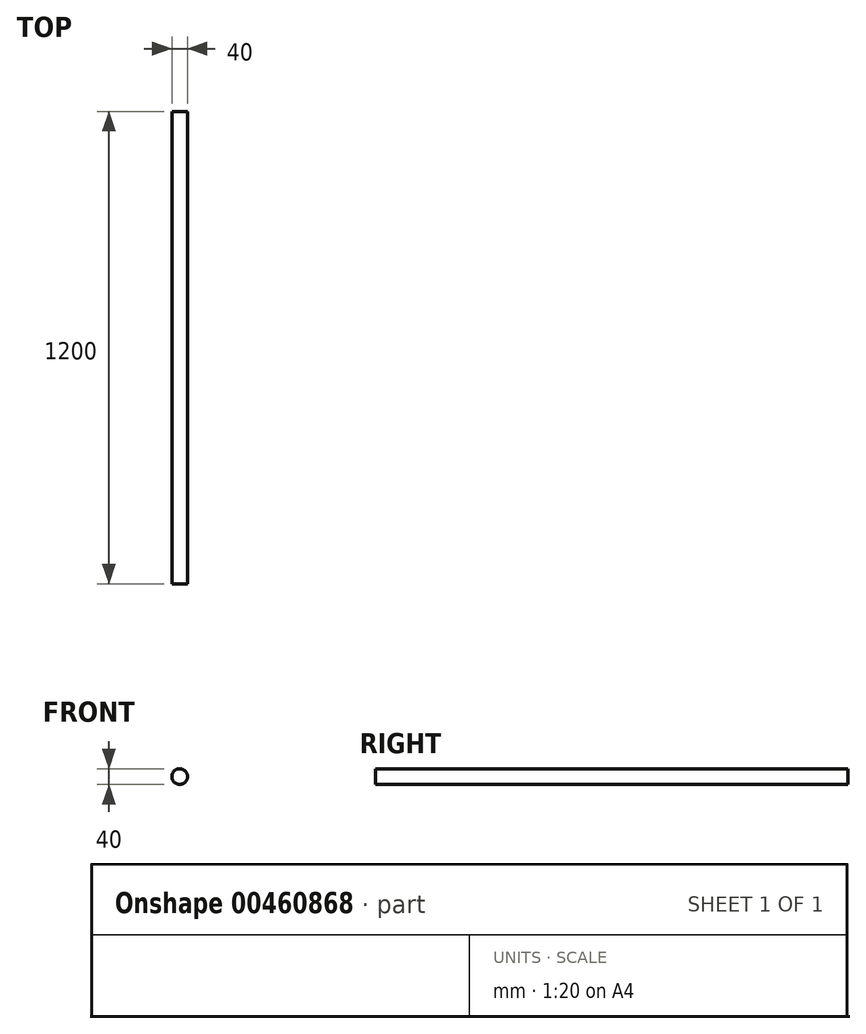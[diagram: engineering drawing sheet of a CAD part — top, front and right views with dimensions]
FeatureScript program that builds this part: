
annotation { "Feature Type Name" : "Feature", "Feature Type Description" : "" }
export const myFeature = defineFeature(function(context is Context, id is Id, definition is map)
    precondition{}
    {
        {
            var Q0;
            Q0=qCreatedBy(makeId("Front.planeOp"),FACE);
            var sketch = newSketch(context, id + "F0", { "sketchPlane" : qUnion([Q0])});
            skCircle(sketch, "E0", {"center": v(21.34, 16.24) * mm, "radius": 20 * mm});
            skSolve(sketch);
        }
        {
            var Q0;
            Q0=makeQuery(id+"F0.imprint","IMPRINT",FACE,{"disambiguationData":[TD([[makeQuery(id+"F0.imprint","IMPRINT",EDGE,{"derivedFrom":sQuery(id+"F0.wireOp",EDGE,"E0")}),1.0]])]});
            extrude(context, id + "F1", {"entities" : qUnion([Q0]), "depth" : 1200 * mm});
        }
    });
